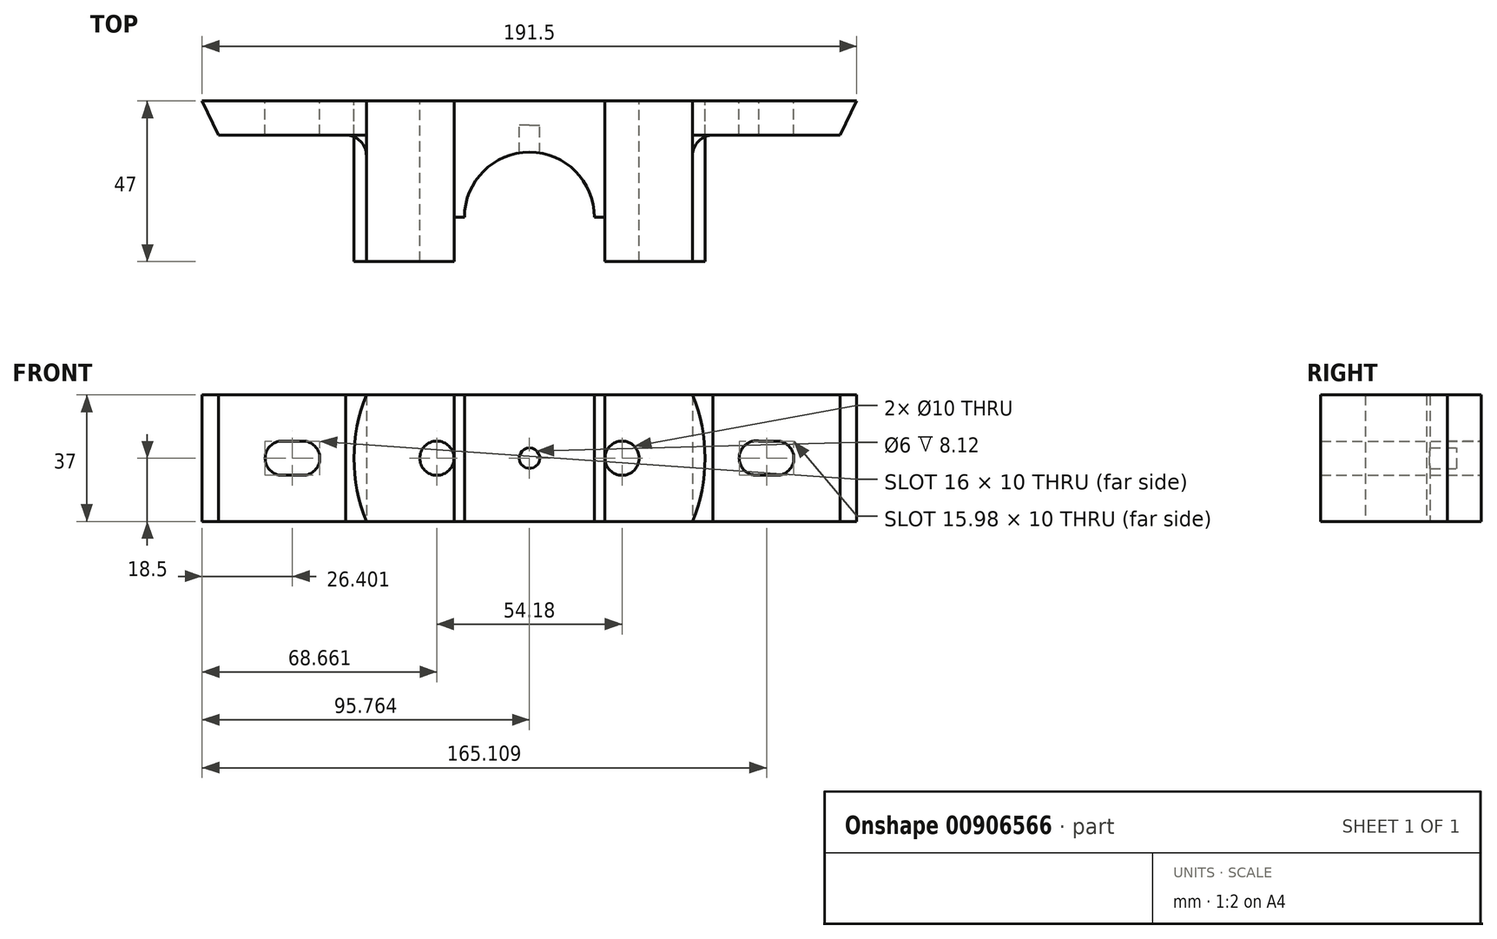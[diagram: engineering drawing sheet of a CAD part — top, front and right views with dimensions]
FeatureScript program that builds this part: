
annotation { "Feature Type Name" : "Feature", "Feature Type Description" : "" }
export const myFeature = defineFeature(function(context is Context, id is Id, definition is map)
    precondition{}
    {
        {
            var Q0;
            Q0=qCreatedBy(makeId("Front.planeOp"),FACE);
            var sketch = newSketch(context, id + "F0", { "sketchPlane" : qUnion([Q0])});
            skLineSegment(sketch, "E0", {"start": v(-110.87, 18) * mm, "end": v(-110.87, -19) * mm});
            skLineSegment(sketch, "E1", {"start": v(-110.87, -19) * mm, "end": v(-99.47, -19) * mm});
            skLineSegment(sketch, "E2", {"start": v(-99.47, -19) * mm, "end": v(-62.84, -19) * mm});
            skLineSegment(sketch, "E3", {"start": v(-62.84, -19) * mm, "end": v(-53.95, -19) * mm});
            skLineSegment(sketch, "E4", {"start": v(-53.95, -19) * mm, "end": v(-37.13, -19) * mm});
            skLineSegment(sketch, "E5", {"start": v(-37.13, -19) * mm, "end": v(-34.13, -19) * mm});
            skLineSegment(sketch, "E6", {"start": v(-34.13, -19) * mm, "end": v(3.87, -19) * mm});
            skLineSegment(sketch, "E7", {"start": v(3.87, -19) * mm, "end": v(23.71, -19) * mm});
            skLineSegment(sketch, "E8", {"start": v(23.71, -19) * mm, "end": v(32.6, -19) * mm});
            skLineSegment(sketch, "E9", {"start": v(32.6, -19) * mm, "end": v(69.23, -19) * mm});
            skLineSegment(sketch, "E10", {"start": v(36.61, -19) * mm, "end": v(69.23, -19) * mm});
            skLineSegment(sketch, "E11", {"start": v(-110.87, 18) * mm, "end": v(36.61, 18) * mm});
            skLineSegment(sketch, "E12", {"start": v(69.23, 18) * mm, "end": v(36.61, 18) * mm});
            skLineSegment(sketch, "E13", {"start": v(69.23, 18) * mm, "end": v(32.6, 18) * mm});
            skLineSegment(sketch, "E14", {"start": v(32.6, 18) * mm, "end": v(23.71, 18) * mm});
            skLineSegment(sketch, "E15", {"start": v(23.71, 18) * mm, "end": v(3.87, 18) * mm});
            skLineSegment(sketch, "E16", {"start": v(3.87, 18) * mm, "end": v(-34.13, 18) * mm});
            skLineSegment(sketch, "E17", {"start": v(-34.13, 18) * mm, "end": v(-37.13, 18) * mm});
            skLineSegment(sketch, "E18", {"start": v(-37.13, 18) * mm, "end": v(-53.95, 18) * mm});
            skLineSegment(sketch, "E19", {"start": v(-53.95, 18) * mm, "end": v(-62.84, 18) * mm});
            skLineSegment(sketch, "E20", {"start": v(-62.84, 18) * mm, "end": v(-99.47, 18) * mm});
            skLineSegment(sketch, "E21", {"start": v(-99.47, 18) * mm, "end": v(-110.87, 18) * mm});
            skLineSegment(sketch, "E22", {"start": v(-99.47, 18) * mm, "end": v(-99.47, -19) * mm});
            skLineSegment(sketch, "E23", {"start": v(-37.13, 18) * mm, "end": v(-37.13, -19) * mm});
            skLineSegment(sketch, "E24", {"start": v(-34.13, 18) * mm, "end": v(-34.13, -19) * mm});
            skLineSegment(sketch, "E25", {"start": v(3.87, 18) * mm, "end": v(3.87, -19) * mm});
            skLineSegment(sketch, "E26", {"start": v(69.23, 18) * mm, "end": v(69.23, -19) * mm});
            skLineSegment(sketch, "E27.0", {"start": v(80.63, 18) * mm, "end": v(80.63, -19) * mm});
            skLineSegment(sketch, "E28", {"start": v(80.63, 18) * mm, "end": v(69.23, 18) * mm});
            skLineSegment(sketch, "E29", {"start": v(80.63, -19) * mm, "end": v(69.23, -19) * mm});
            skArc(sketch, "E30", {"start": v(-62.84, 18) * mm, "mid": v(-66.47, -0.5) * mm, "end": v(-62.84, -19) * mm});
            skArc(sketch, "E31", {"start": v(-53.95, 18) * mm, "mid": v(-58.13, -0.5) * mm, "end": v(-53.95, -19) * mm});
            skArc(sketch, "E32", {"start": v(32.6, -19) * mm, "mid": v(36.23, -0.5) * mm, "end": v(32.6, 18) * mm});
            skArc(sketch, "E33", {"start": v(23.71, -19) * mm, "mid": v(27.9, -0.5) * mm, "end": v(23.71, 18) * mm});
            skLineSegment(sketch, "E34", {"start": v(6.9, 18) * mm, "end": v(6.9, -19) * mm});
            skPoint(sketch, "E35.startSnap0", {"position": v(-15.13, 18) * mm});
            skPoint(sketch, "E36.endSnap0", {"position": v(-99.47, -0.5) * mm});
            skArc(sketch, "E37", {"start": v(57.23, -5.5) * mm, "mid": v(62.23, -0.5) * mm, "end": v(57.23, 4.5) * mm});
            skArc(sketch, "E38", {"start": v(-87.47, 4.5) * mm, "mid": v(-92.47, -0.5) * mm, "end": v(-87.47, -5.5) * mm});
            skCircle(sketch, "E39", {"center": v(-42.2, -0.5) * mm, "radius": 5 * mm});
            skCircle(sketch, "E40", {"center": v(11.97, -0.5) * mm, "radius": 5 * mm});
            skCircle(sketch, "E41", {"center": v(-15.1, -0.5) * mm, "radius": 3 * mm});
            skLineSegment(sketch, "E42", {"start": v(-87.47, 4.5) * mm, "end": v(-81.47, 4.5) * mm});
            skLineSegment(sketch, "E43", {"start": v(-81.47, -5.5) * mm, "end": v(-87.47, -5.5) * mm});
            skLineSegment(sketch, "E44", {"start": v(57.23, 4.5) * mm, "end": v(51.23, 4.5) * mm});
            skLineSegment(sketch, "E45", {"start": v(51.23, -5.5) * mm, "end": v(57.23, -5.5) * mm});
            skArc(sketch, "E46", {"start": v(-81.47, -5.5) * mm, "mid": v(-76.47, -0.5) * mm, "end": v(-81.47, 4.5) * mm});
            skArc(sketch, "E47", {"start": v(52.05, 4.5) * mm, "mid": v(46.25, -0.05) * mm, "end": v(51.23, -5.5) * mm});
            skLineSegment(sketch, "E48", {"start": v(-42.2, -0.5) * mm, "end": v(-37.13, -0.5) * mm});
            skLineSegment(sketch, "E49", {"start": v(11.97, -0.5) * mm, "end": v(6.9, -0.5) * mm});
            skSolve(sketch);
        }
        {
            var Q0;
            Q0=makeQuery(id+"F0.imprint","IMPRINT",FACE,{"disambiguationData":[TD([[makeQuery(id+"F0.imprint","IMPRINT",EDGE,{"derivedFrom":sQuery(id+"F0.wireOp",EDGE,"E2")}),1.0]])]});
            var Q1;
            Q1=makeQuery(id+"F0.imprint","IMPRINT",FACE,{"disambiguationData":[TD([[makeQuery(id+"F0.imprint","IMPRINT",EDGE,{"derivedFrom":sQuery(id+"F0.wireOp",EDGE,"E9")}),1.0]])]});
            var Q2;
            Q2=makeQuery(id+"F0.imprint","IMPRINT",FACE,{"disambiguationData":[TD([[makeQuery(id+"F0.imprint","IMPRINT",EDGE,{"derivedFrom":sQuery(id+"F0.wireOp",EDGE,"E26")}),1.0]])]});
            var Q3;
            Q3=makeQuery(id+"F0.imprint","IMPRINT",FACE,{"disambiguationData":[TD([[makeQuery(id+"F0.imprint","IMPRINT",EDGE,{"derivedFrom":sQuery(id+"F0.wireOp",EDGE,"E0")}),1.0]])]});
            extrude(context, id + "F1", {"entities" : qUnion([Q0, Q1, Q2, Q3]), "depth" : 10 * mm, "offsetDistance" : 25.4 * mm});
        }
        {
            var Q0;
            Q0=makeQuery(id+"F0.imprint","IMPRINT",FACE,{"disambiguationData":[TD([[makeQuery(id+"F0.imprint","IMPRINT",EDGE,{"derivedFrom":sQuery(id+"F0.wireOp",EDGE,"E3")}),1.0]])]});
            var Q1;
            Q1=makeQuery(id+"F0.imprint","IMPRINT",FACE,{"disambiguationData":[TD([[makeQuery(id+"F0.imprint","IMPRINT",EDGE,{"derivedFrom":sQuery(id+"F0.wireOp",EDGE,"E8")}),1.0]])]});
            var Q2;
            Q2=makeQuery(id+"F0.imprint","IMPRINT",FACE,{"disambiguationData":[TD([[makeQuery(id+"F0.imprint","IMPRINT",EDGE,{"derivedFrom":sQuery(id+"F0.wireOp",EDGE,"E4")}),1.0]])]});
            var Q3;
            {var subQ1=sQuery(id+"F0.wireOp",EDGE,"E33");Q3=makeQuery(id+"F0.imprint","IMPRINT",FACE,{"disambiguationData":[TD([[makeQuery(id+"F0.imprint","IMPRINT",EDGE,{"derivedFrom":subQ1}),1.0]])]});}
            extrude(context, id + "F2", {"entities" : qUnion([Q0, Q1, Q2, Q3]), "depth" : 47 * mm, "offsetDistance" : 25.4 * mm});
        }
        {
            var Q0;
            Q0=makeQuery(id+"F0.imprint","IMPRINT",FACE,{"disambiguationData":[TD([[makeQuery(id+"F0.imprint","IMPRINT",EDGE,{"derivedFrom":sQuery(id+"F0.wireOp",EDGE,"E5")}),1.0]])]});
            var Q1;
            {var subQ0=sQuery(id+"F0.wireOp",EDGE,"E25");Q1=makeQuery(id+"F0.imprint","IMPRINT",FACE,{"disambiguationData":[TD([[makeQuery(id+"F0.imprint","IMPRINT",EDGE,{"derivedFrom":subQ0}),1.0]])]});}
            var Q2;
            Q2=makeQuery(id+"F0.imprint","IMPRINT",FACE,{"disambiguationData":[TD([[makeQuery(id+"F0.imprint","IMPRINT",EDGE,{"derivedFrom":sQuery(id+"F0.wireOp",EDGE,"E6")}),1.0]])]});
            extrude(context, id + "F3", {"entities" : qUnion([Q0, Q1, Q2]), "depth" : 34 * mm, "offsetDistance" : 25.4 * mm});
        }
        {
            var Q0;
            Q0=makeQuery(id+"F3.opExtrude","SWEPT_FACE",FACE,{"disambiguationData":[OSD([sQuery(id+"F0.wireOp",EDGE,"E5"),sQuery(id+"F0.wireOp",EDGE,"E6"),sQuery(id+"F0.wireOp",EDGE,"E7")])]});
            var sketch = newSketch(context, id + "F4", { "sketchPlane" : qUnion([Q0])});
            skLineSegment(sketch, "E50", {"start": v(6.9, 34) * mm, "end": v(3.9, 34) * mm});
            skLineSegment(sketch, "E51", {"start": v(-37.13, 34) * mm, "end": v(-34.13, 34) * mm});
            skArc(sketch, "E52", {"start": v(-34.13, 34) * mm, "mid": v(-15.12, 14.99) * mm, "end": v(3.9, 34) * mm});
            skSolve(sketch);
        }
        {
            var Q0;
            {var subQ0=sQuery(id+"F4.wireOp",EDGE,"E52");Q0=makeQuery(id+"F4.imprint","IMPRINT",FACE,{"disambiguationData":[TD([[makeQuery(id+"F4.imprint","IMPRINT",EDGE,{"derivedFrom":subQ0}),1.0]])]});}
            extrude(context, id + "F5", {"entities" : qUnion([Q0]), "operationType" : NewBodyOperationType.REMOVE, "oppositeDirection" : true, "depth" : 127 * mm, "offsetDistance" : 25.4 * mm});
        }
        {
            var Q0;
            Q0=makeQuery(id+"F1.opExtrude","SWEPT_FACE",FACE,{"disambiguationData":[OSD([sQuery(id+"F0.wireOp",EDGE,"E1"),sQuery(id+"F0.wireOp",EDGE,"E2")])]});
            var sketch = newSketch(context, id + "F6", { "sketchPlane" : qUnion([Q0])});
            skLineSegment(sketch, "E53", {"start": v(-62.84, 10) * mm, "end": v(-99.47, 10) * mm});
            skLineSegment(sketch, "E54", {"start": v(-62.84, 0) * mm, "end": v(-62.84, 10) * mm});
            skLineSegment(sketch, "E55", {"start": v(-110.87, 0) * mm, "end": v(-106.04, 10) * mm});
            skSolve(sketch);
        }
        {
            var Q0;
            {var subQ0=sQuery(id+"F6.wireOp",EDGE,"E55");Q0=makeQuery(id+"F6.imprint","IMPRINT",FACE,{"disambiguationData":[TD([[makeQuery(id+"F6.imprint","IMPRINT",EDGE,{"derivedFrom":subQ0}),1.0]])]});}
            extrude(context, id + "F7", {"entities" : qUnion([Q0]), "operationType" : NewBodyOperationType.REMOVE, "oppositeDirection" : true, "depth" : 101.6 * mm, "offsetDistance" : 25.4 * mm});
        }
        {
            var Q0;
            Q0=makeQuery(id+"F1.opExtrude","SWEPT_FACE",FACE,{"disambiguationData":[OSD([sQuery(id+"F0.wireOp",EDGE,"E9"),sQuery(id+"F0.wireOp",EDGE,"E10"),sQuery(id+"F0.wireOp",EDGE,"E29")])]});
            var sketch = newSketch(context, id + "F8", { "sketchPlane" : qUnion([Q0])});
            skLineSegment(sketch, "E56", {"start": v(80.63, 0) * mm, "end": v(75.8, 10) * mm});
            skSolve(sketch);
        }
        {
            var Q0;
            {var subQ0=sQuery(id+"F8.wireOp",EDGE,"E56");Q0=makeQuery(id+"F8.imprint","IMPRINT",FACE,{"disambiguationData":[TD([[makeQuery(id+"F8.imprint","IMPRINT",EDGE,{"derivedFrom":subQ0}),-1.0]])]});}
            extrude(context, id + "F9", {"entities" : qUnion([Q0]), "operationType" : NewBodyOperationType.REMOVE, "oppositeDirection" : true, "depth" : 101.6 * mm, "offsetDistance" : 25.4 * mm});
        }
        {
            var Q0;
            Q0=makeQuery(id+"F1.opExtrude","SWEPT_FACE",FACE,{"disambiguationData":[OSD([sQuery(id+"F0.wireOp",EDGE,"E9"),sQuery(id+"F0.wireOp",EDGE,"E10"),sQuery(id+"F0.wireOp",EDGE,"E29")])]});
            var sketch = newSketch(context, id + "F10", { "sketchPlane" : qUnion([Q0])});
            skLineSegment(sketch, "E57", {"start": v(32.6, 16) * mm, "end": v(32.6, 23.02) * mm});
            skLineSegment(sketch, "E58", {"start": v(38.6, 10) * mm, "end": v(44.14, 10) * mm});
            skPoint(sketch, "E59.visualSharp", {"position": v(32.6, 10) * mm});
            skArc(sketch, "E59.filletArc", {"start": v(32.6, 16) * mm, "mid": v(34.36, 11.76) * mm, "end": v(38.6, 10) * mm});
            skLineSegment(sketch, "E60", {"start": v(32.6, 10) * mm, "end": v(32.6, 16) * mm});
            skLineSegment(sketch, "E61", {"start": v(32.6, 10) * mm, "end": v(38.6, 10) * mm});
            skSolve(sketch);
        }
        {
            var Q0;
            Q0=makeQuery(id+"F10.imprint","IMPRINT",FACE,{"disambiguationData":[TD([[makeQuery(id+"F10.imprint","IMPRINT",EDGE,{"derivedFrom":sQuery(id+"F10.wireOp",EDGE,"E59.filletArc")}),-1.0]])]});
            extrude(context, id + "F11", {"entities" : qUnion([Q0]), "oppositeDirection" : true, "depth" : 37 * mm, "offsetDistance" : 25.4 * mm});
        }
        {
            var Q0;
            Q0=makeQuery(id+"F1.opExtrude","SWEPT_FACE",FACE,{"disambiguationData":[OSD([sQuery(id+"F0.wireOp",EDGE,"E1"),sQuery(id+"F0.wireOp",EDGE,"E2")])]});
            var sketch = newSketch(context, id + "F12", { "sketchPlane" : qUnion([Q0])});
            skLineSegment(sketch, "E62", {"start": v(-62.84, 16) * mm, "end": v(-62.84, 18.8) * mm});
            skLineSegment(sketch, "E63", {"start": v(-68.84, 10) * mm, "end": v(-74.1, 10) * mm});
            skPoint(sketch, "E64.visualSharp", {"position": v(-62.84, 10) * mm});
            skArc(sketch, "E64.filletArc", {"start": v(-68.84, 10) * mm, "mid": v(-64.6, 11.76) * mm, "end": v(-62.84, 16) * mm});
            skLineSegment(sketch, "E65", {"start": v(-68.84, 10) * mm, "end": v(-62.84, 10) * mm});
            skLineSegment(sketch, "E66", {"start": v(-62.84, 16) * mm, "end": v(-62.84, 10) * mm});
            skSolve(sketch);
        }
        {
            var Q0;
            Q0=makeQuery(id+"F12.imprint","IMPRINT",FACE,{"disambiguationData":[TD([[makeQuery(id+"F12.imprint","IMPRINT",EDGE,{"derivedFrom":sQuery(id+"F12.wireOp",EDGE,"E64.filletArc")}),-1.0]])]});
            extrude(context, id + "F13", {"entities" : qUnion([Q0]), "oppositeDirection" : true, "depth" : 37 * mm, "offsetDistance" : 25.4 * mm});
        }
        {
            var Q0;
            Q0=makeQuery(id+"F0.imprint","IMPRINT",FACE,{"disambiguationData":[TD([[makeQuery(id+"F0.imprint","IMPRINT",EDGE,{"derivedFrom":sQuery(id+"F0.wireOp",EDGE,"E41")}),1.0]])]});
            extrude(context, id + "F14", {"entities" : qUnion([Q0]), "operationType" : NewBodyOperationType.ADD, "depth" : 7.11 * mm, "offsetDistance" : 25.4 * mm});
        }
    });
